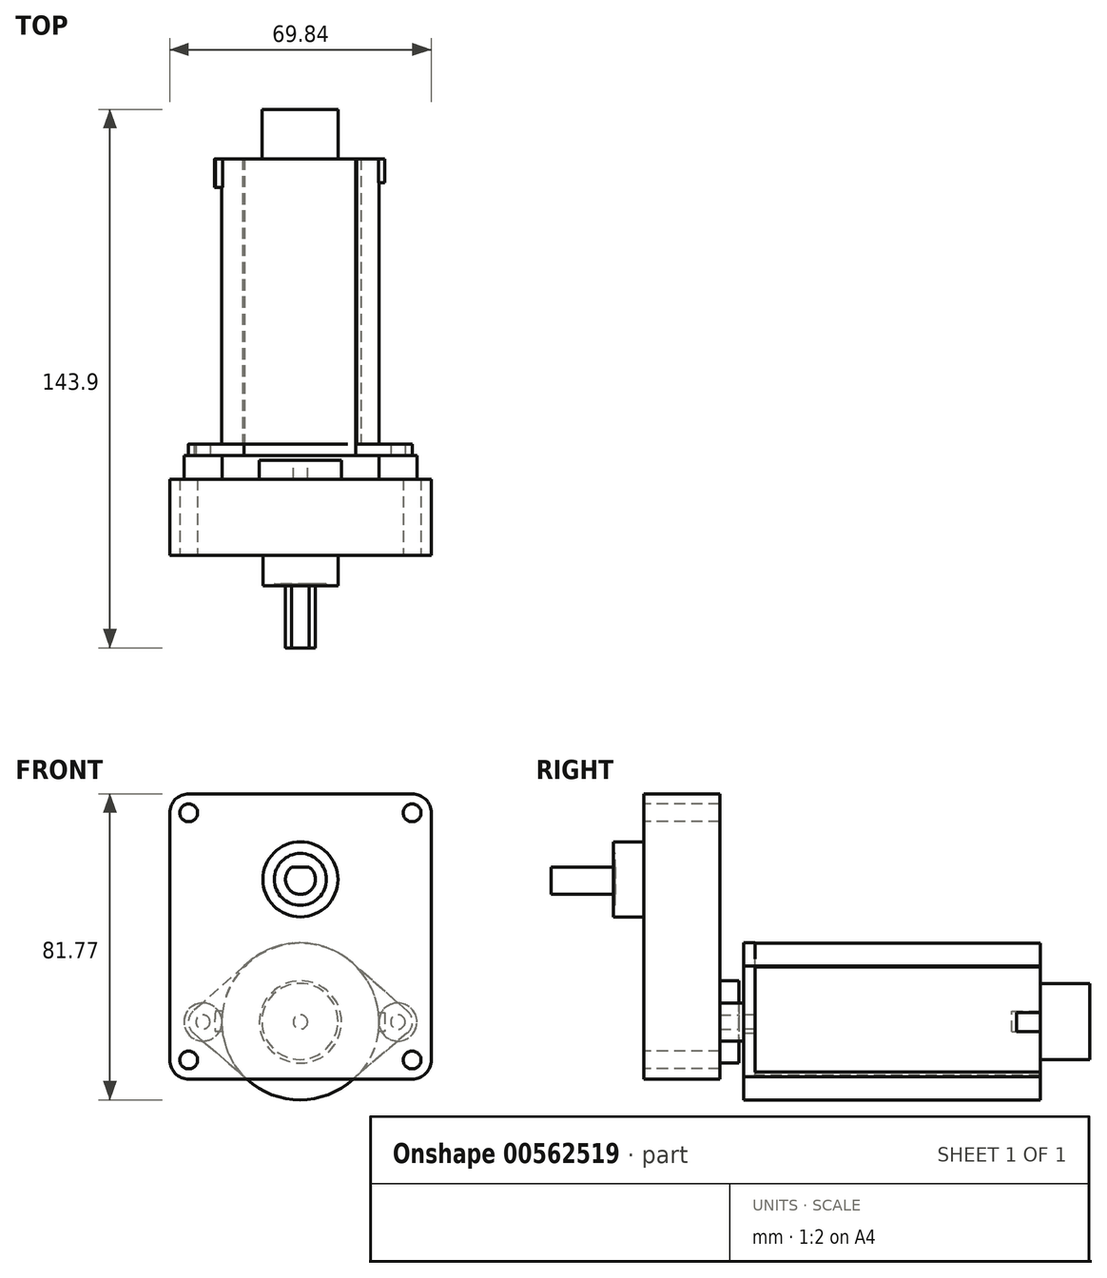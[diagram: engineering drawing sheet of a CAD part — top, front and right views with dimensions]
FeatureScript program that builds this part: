
annotation { "Feature Type Name" : "Feature", "Feature Type Description" : "" }
export const myFeature = defineFeature(function(context is Context, id is Id, definition is map)
    precondition{}
    {
        {
            var Q0;
            Q0=qCreatedBy(makeId("Front.planeOp"),FACE);
            var sketch = newSketch(context, id + "F0", { "sketchPlane" : qUnion([Q0])});
            skLineSegment(sketch, "E0.bottom", {"start": v(34.93, -38.1) * mm, "end": v(-34.92, -38.1) * mm});
            skLineSegment(sketch, "E0.top", {"start": v(34.92, 38.1) * mm, "end": v(-34.93, 38.1) * mm});
            skLineSegment(sketch, "E0.left", {"start": v(34.93, -38.1) * mm, "end": v(34.92, 38.1) * mm});
            skLineSegment(sketch, "E0.right", {"start": v(-34.92, -38.1) * mm, "end": v(-34.93, 38.1) * mm});
            skPoint(sketch, "E0.middle", {"position": v(0, 0) * mm});
            skSolve(sketch);
        }
        {
            var Q0;
            Q0=qSketchRegion(id+"F0",true);
            extrude(context, id + "F1", {"entities" : qUnion([Q0]), "depth" : 20.32 * mm, "offsetDistance" : 25.4 * mm});
        }
        {
            var Q0;
            Q0=makeQuery(id+"F1.opExtrude","SWEPT_EDGE",EDGE,{"disambiguationData":[OSD([sQuery(id+"F0.wireOp",EDGE,"E0.top"),sQuery(id+"F0.wireOp",EDGE,"E0.right")])]});
            var Q1;
            Q1=makeQuery(id+"F1.opExtrude","SWEPT_EDGE",EDGE,{"disambiguationData":[OSD([sQuery(id+"F0.wireOp",EDGE,"E0.bottom"),sQuery(id+"F0.wireOp",EDGE,"E0.right")])]});
            var Q2;
            Q2=makeQuery(id+"F1.opExtrude","SWEPT_EDGE",EDGE,{"disambiguationData":[OSD([sQuery(id+"F0.wireOp",EDGE,"E0.bottom"),sQuery(id+"F0.wireOp",EDGE,"E0.left")])]});
            var Q3;
            Q3=makeQuery(id+"F1.opExtrude","SWEPT_EDGE",EDGE,{"disambiguationData":[OSD([sQuery(id+"F0.wireOp",EDGE,"E0.top"),sQuery(id+"F0.wireOp",EDGE,"E0.left")])]});
            fillet(context, id + "F2", {"entities" : qUnion([Q0, Q1, Q2, Q3]), "radius" : 5.08 * mm, "tangentPropagation" : true, "allowEdgeOverflow" : false});
        }
        {
            var Q0;
            Q0=makeQuery(id+"F1.opExtrude","CAP_FACE",FACE,{"disambiguationData":[OSD([sQuery(id+"F0.wireOp",EDGE,"E0.bottom"),sQuery(id+"F0.wireOp",EDGE,"E0.top"),sQuery(id+"F0.wireOp",EDGE,"E0.left"),sQuery(id+"F0.wireOp",EDGE,"E0.right")])],"isStart":false});
            var sketch = newSketch(context, id + "F3", { "sketchPlane" : qUnion([Q0])});
            skPoint(sketch, "E1.middle", {"position": v(0, 0) * mm});
            skCircle(sketch, "E2", {"center": v(-29.84, 33.02) * mm, "radius": 2.37 * mm});
            skCircle(sketch, "E3", {"center": v(29.84, 33.02) * mm, "radius": 2.37 * mm});
            skCircle(sketch, "E4", {"center": v(29.84, -33.02) * mm, "radius": 2.37 * mm});
            skCircle(sketch, "E5", {"center": v(-29.84, -33.02) * mm, "radius": 2.37 * mm});
            skSolve(sketch);
        }
        {
            var Q0;
            Q0=makeQuery(id+"F3.imprint","IMPRINT",FACE,{"disambiguationData":[TD([[makeQuery(id+"F3.imprint","IMPRINT",EDGE,{"derivedFrom":sQuery(id+"F3.wireOp",EDGE,"E2")}),1.0]])]});
            var Q1;
            Q1=makeQuery(id+"F3.imprint","IMPRINT",FACE,{"disambiguationData":[TD([[makeQuery(id+"F3.imprint","IMPRINT",EDGE,{"derivedFrom":sQuery(id+"F3.wireOp",EDGE,"E3")}),1.0]])]});
            var Q2;
            Q2=makeQuery(id+"F3.imprint","IMPRINT",FACE,{"disambiguationData":[TD([[makeQuery(id+"F3.imprint","IMPRINT",EDGE,{"derivedFrom":sQuery(id+"F3.wireOp",EDGE,"E5")}),1.0]])]});
            var Q3;
            Q3=makeQuery(id+"F3.imprint","IMPRINT",FACE,{"disambiguationData":[TD([[makeQuery(id+"F3.imprint","IMPRINT",EDGE,{"derivedFrom":sQuery(id+"F3.wireOp",EDGE,"E4")}),1.0]])]});
            extrude(context, id + "F4", {"entities" : qUnion([Q0, Q1, Q2, Q3]), "operationType" : NewBodyOperationType.REMOVE, "endBound" : BoundingType.THROUGH_ALL, "oppositeDirection" : true, "depth" : 25.4 * mm, "offsetDistance" : 25.4 * mm});
        }
        {
            var Q0;
            Q0=makeQuery(id+"F1.opExtrude","CAP_FACE",FACE,{"disambiguationData":[OSD([sQuery(id+"F0.wireOp",EDGE,"E0.bottom"),sQuery(id+"F0.wireOp",EDGE,"E0.top"),sQuery(id+"F0.wireOp",EDGE,"E0.left"),sQuery(id+"F0.wireOp",EDGE,"E0.right")])],"isStart":false});
            var sketch = newSketch(context, id + "F5", { "sketchPlane" : qUnion([Q0])});
            skLineSegment(sketch, "E6", {"start": v(0, 0) * mm, "end": v(0, 38.1) * mm, "construction": true});
            skLineSegment(sketch, "E7", {"start": v(0, 15.24) * mm, "end": v(34.92, 15.24) * mm, "construction": true});
            skCircle(sketch, "E8", {"center": v(0, 15.24) * mm, "radius": 10.03 * mm});
            skSolve(sketch);
        }
        {
            var Q0;
            Q0=qSketchRegion(id+"F5",true);
            extrude(context, id + "F6", {"entities" : qUnion([Q0]), "operationType" : NewBodyOperationType.ADD, "depth" : 8.13 * mm, "offsetDistance" : 25.4 * mm});
        }
        {
            var Q0;
            Q0=makeQuery(id+"F6.opExtrude","CAP_FACE",FACE,{"disambiguationData":[OSD([sQuery(id+"F5.wireOp",EDGE,"E8")])],"isStart":false});
            var sketch = newSketch(context, id + "F7", { "sketchPlane" : qUnion([Q0])});
            skCircle(sketch, "E9", {"center": v(0, 15.24) * mm, "radius": 6.95 * mm});
            skSolve(sketch);
        }
        {
            var Q0;
            Q0=qSketchRegion(id+"F7",true);
            extrude(context, id + "F8", {"entities" : qUnion([Q0]), "operationType" : NewBodyOperationType.REMOVE, "oppositeDirection" : true, "depth" : 0.5 * mm, "offsetDistance" : 25.4 * mm});
        }
        {
            var Q0;
            Q0=makeQuery(id+"F8.boolean.opBoolean","COPY",FACE,{"derivedFrom":makeQuery(id+"F8.opExtrude","CAP_FACE",FACE,{"disambiguationData":[OSD([sQuery(id+"F7.wireOp",EDGE,"E9")])],"isStart":false})});
            var sketch = newSketch(context, id + "F9", { "sketchPlane" : qUnion([Q0])});
            skArc(sketch, "E10", {"start": v(-2.35, 18.48) * mm, "mid": v(0, 11.24) * mm, "end": v(2.35, 18.48) * mm});
            skLineSegment(sketch, "E11", {"start": v(-2.35, 18.48) * mm, "end": v(2.35, 18.48) * mm});
            skSolve(sketch);
        }
        {
            var Q0;
            Q0=makeQuery(id+"F9.imprint","IMPRINT",FACE,{"disambiguationData":[TD([[makeQuery(id+"F9.imprint","IMPRINT",EDGE,{"derivedFrom":sQuery(id+"F9.wireOp",EDGE,"E10")}),1.0]])]});
            extrude(context, id + "F10", {"entities" : qUnion([Q0]), "operationType" : NewBodyOperationType.ADD, "depth" : 17.14 * mm, "offsetDistance" : 25.4 * mm});
        }
        {
            var Q0;
            Q0=makeQuery(id+"F1.opExtrude","CAP_FACE",FACE,{"disambiguationData":[OSD([sQuery(id+"F0.wireOp",EDGE,"E0.bottom"),sQuery(id+"F0.wireOp",EDGE,"E0.top"),sQuery(id+"F0.wireOp",EDGE,"E0.left"),sQuery(id+"F0.wireOp",EDGE,"E0.right")])],"isStart":true});
            var sketch = newSketch(context, id + "F11", { "sketchPlane" : qUnion([Q0])});
            skLineSegment(sketch, "E12", {"start": v(-34.93, -22.86) * mm, "end": v(34.92, -22.86) * mm, "construction": true});
            skCircle(sketch, "E13", {"center": v(0, -22.86) * mm, "radius": 10.99 * mm});
            skLineSegment(sketch, "E14", {"start": v(26.03, -38.1) * mm, "end": v(26.04, 38.1) * mm, "construction": true});
            skLineSegment(sketch, "E15", {"start": v(-26.04, -38.1) * mm, "end": v(-26.04, 38.1) * mm, "construction": true});
            skCircle(sketch, "E16", {"center": v(-26.04, -22.86) * mm, "radius": 5.08 * mm});
            skCircle(sketch, "E17", {"center": v(26.03, -22.86) * mm, "radius": 5.08 * mm});
            skSolve(sketch);
        }
        {
            var Q0;
            Q0=makeQuery(id+"F11.imprint","IMPRINT",FACE,{"disambiguationData":[TD([[makeQuery(id+"F11.imprint","IMPRINT",EDGE,{"derivedFrom":sQuery(id+"F11.wireOp",EDGE,"E13")}),1.0]])]});
            extrude(context, id + "F12", {"entities" : qUnion([Q0]), "operationType" : NewBodyOperationType.ADD, "depth" : 5.08 * mm, "offsetDistance" : 25.4 * mm});
        }
        {
            var Q0;
            Q0=makeQuery(id+"F11.imprint","IMPRINT",FACE,{"disambiguationData":[TD([[makeQuery(id+"F11.imprint","IMPRINT",EDGE,{"derivedFrom":sQuery(id+"F11.wireOp",EDGE,"E17")}),1.0]])]});
            extrude(context, id + "F13", {"entities" : qUnion([Q0]), "operationType" : NewBodyOperationType.ADD, "depth" : 6.35 * mm, "offsetDistance" : 25.4 * mm});
        }
        {
            var Q0;
            Q0=makeQuery(id+"F11.imprint","IMPRINT",FACE,{"disambiguationData":[TD([[makeQuery(id+"F11.imprint","IMPRINT",EDGE,{"derivedFrom":sQuery(id+"F11.wireOp",EDGE,"E16")}),1.0]])]});
            extrude(context, id + "F14", {"entities" : qUnion([Q0]), "operationType" : NewBodyOperationType.ADD, "depth" : 6.35 * mm, "offsetDistance" : 25.4 * mm});
        }
        {
            var Q0;
            Q0=makeQuery(id+"F12.opExtrude","CAP_FACE",FACE,{"disambiguationData":[OSD([sQuery(id+"F11.wireOp",EDGE,"E13")])],"isStart":false});
            var sketch = newSketch(context, id + "F15", { "sketchPlane" : qUnion([Q0])});
            skCircle(sketch, "E18", {"center": v(0, -22.86) * mm, "radius": 1.9 * mm});
            skSolve(sketch);
        }
        {
            var Q0;
            Q0=makeQuery(id+"F15.imprint","IMPRINT",FACE,{"disambiguationData":[TD([[makeQuery(id+"F15.imprint","IMPRINT",EDGE,{"derivedFrom":sQuery(id+"F15.wireOp",EDGE,"E18")}),1.0]])]});
            extrude(context, id + "F16", {"entities" : qUnion([Q0]), "operationType" : NewBodyOperationType.REMOVE, "oppositeDirection" : true, "depth" : 5.08 * mm, "offsetDistance" : 25.4 * mm});
        }
        {
            var Q0;
            Q0=makeQuery(id+"F14.opExtrude","CAP_FACE",FACE,{"disambiguationData":[OSD([sQuery(id+"F11.wireOp",EDGE,"E16")])],"isStart":false});
            var sketch = newSketch(context, id + "F17", { "sketchPlane" : qUnion([Q0])});
            skCircle(sketch, "E19", {"center": v(-26.04, -22.86) * mm, "radius": 1.59 * mm});
            skCircle(sketch, "E20", {"center": v(26.03, -22.86) * mm, "radius": 1.59 * mm});
            skSolve(sketch);
        }
        {
            var Q0;
            Q0=makeQuery(id+"F17.imprint","IMPRINT",FACE,{"disambiguationData":[TD([[makeQuery(id+"F17.imprint","IMPRINT",EDGE,{"derivedFrom":sQuery(id+"F17.wireOp",EDGE,"E19")}),-1.0]])]});
            var sketch = newSketch(context, id + "F18", { "sketchPlane" : qUnion([Q0])});
            skCircle(sketch, "E21", {"center": v(-26.04, -22.86) * mm, "radius": 1.93 * mm});
            skCircle(sketch, "E22", {"center": v(26.03, -22.86) * mm, "radius": 1.89 * mm});
            skArc(sketch, "E23", {"start": v(-28.58, -19.92) * mm, "mid": v(-29.92, -22.89) * mm, "end": v(-28.54, -25.83) * mm});
            skArc(sketch, "E24", {"start": v(28.38, -25.96) * mm, "mid": v(29.92, -23.01) * mm, "end": v(28.62, -19.95) * mm});
            skLineSegment(sketch, "E25", {"start": v(-28.58, -19.92) * mm, "end": v(-14.74, -7.93) * mm});
            skLineSegment(sketch, "E26", {"start": v(-28.54, -25.83) * mm, "end": v(-14.74, -37.48) * mm});
            skArc(sketch, "E27.trimOffspring", {"start": v(-14.74, -37.48) * mm, "mid": v(0.08, -43.67) * mm, "end": v(14.94, -37.55) * mm});
            skPoint(sketch, "E28.center.orphan", {"position": v(0, -22.82) * mm});
            skPoint(sketch, "E29.end.orphan", {"position": v(15.07, -7.93) * mm});
            skPoint(sketch, "E30.end.orphan", {"position": v(15.07, -37.71) * mm});
            skLineSegment(sketch, "E31", {"start": v(28.38, -25.96) * mm, "end": v(14.94, -37.55) * mm});
            skLineSegment(sketch, "E32", {"start": v(15.03, -7.96) * mm, "end": v(28.62, -19.95) * mm});
            skArc(sketch, "E33.trimOffspring", {"start": v(15.03, -7.96) * mm, "mid": v(0.15, -1.74) * mm, "end": v(-14.74, -7.93) * mm});
            skSolve(sketch);
        }
        {
            var Q0;
            Q0=qSketchRegion(id+"F18",true);
            extrude(context, id + "F19", {"entities" : qUnion([Q0]), "operationType" : NewBodyOperationType.ADD, "depth" : 3.05 * mm, "offsetDistance" : 25.4 * mm});
        }
        {
            var Q0;
            Q0=makeQuery(id+"F19.opExtrude","CAP_FACE",FACE,{"disambiguationData":[OSD([sQuery(id+"F18.wireOp",EDGE,"E21"),sQuery(id+"F18.wireOp",EDGE,"E22"),sQuery(id+"F18.wireOp",EDGE,"E23"),sQuery(id+"F18.wireOp",EDGE,"E24"),sQuery(id+"F18.wireOp",EDGE,"E25"),sQuery(id+"F18.wireOp",EDGE,"E26"),sQuery(id+"F18.wireOp",EDGE,"E27.trimOffspring"),sQuery(id+"F18.wireOp",EDGE,"E31"),sQuery(id+"F18.wireOp",EDGE,"E32"),sQuery(id+"F18.wireOp",EDGE,"E33.trimOffspring")])],"isStart":false});
            var sketch = newSketch(context, id + "F20", { "sketchPlane" : qUnion([Q0])});
            skCircle(sketch, "E34", {"center": v(0, -22.86) * mm, "radius": 21.01 * mm});
            skCircle(sketch, "E35", {"center": v(-26.04, -22.86) * mm, "radius": 3.7 * mm});
            skCircle(sketch, "E36", {"center": v(26.03, -22.86) * mm, "radius": 3.68 * mm});
            skSolve(sketch);
        }
        {
            var Q0;
            {var subQ0=makeQuery(id+"F19.opExtrude","CAP_EDGE",EDGE,{"disambiguationData":[OSD([sQuery(id+"F18.wireOp",EDGE,"E27.trimOffspring")])],"isStart":false});Q0=makeQuery(id+"F20.imprint","IMPRINT",FACE,{"disambiguationData":[TD([[makeQuery(id+"F20.imprint","IMPRINT",EDGE,{"derivedFrom":subQ0}),1.0]])]});}
            extrude(context, id + "F21", {"entities" : qUnion([Q0]), "operationType" : NewBodyOperationType.ADD, "depth" : 76.2 * mm, "offsetDistance" : 25.4 * mm});
        }
        {
            var Q0;
            Q0=makeQuery(id+"F21.opExtrude","CAP_FACE",FACE,{"disambiguationData":[OSD([sQuery(id+"F18.wireOp",EDGE,"E25"),sQuery(id+"F18.wireOp",EDGE,"E26"),sQuery(id+"F18.wireOp",EDGE,"E27.trimOffspring"),sQuery(id+"F18.wireOp",EDGE,"E31"),sQuery(id+"F18.wireOp",EDGE,"E33.trimOffspring"),sQuery(id+"F20.wireOp",EDGE,"E34")])],"isStart":false});
            var sketch = newSketch(context, id + "F22", { "sketchPlane" : qUnion([Q0])});
            skCircle(sketch, "E37", {"center": v(0.13, -22.7) * mm, "radius": 10.16 * mm});
            skSolve(sketch);
        }
        {
            var Q0;
            Q0=qSketchRegion(id+"F22",true);
            extrude(context, id + "F23", {"entities" : qUnion([Q0]), "operationType" : NewBodyOperationType.ADD, "depth" : 13.2 * mm, "offsetDistance" : 25.4 * mm});
        }
        {
            var Q0;
            Q0=makeQuery(id+"F21.opExtrude","CAP_FACE",FACE,{"disambiguationData":[OSD([sQuery(id+"F18.wireOp",EDGE,"E25"),sQuery(id+"F18.wireOp",EDGE,"E26"),sQuery(id+"F18.wireOp",EDGE,"E27.trimOffspring"),sQuery(id+"F18.wireOp",EDGE,"E31"),sQuery(id+"F18.wireOp",EDGE,"E33.trimOffspring"),sQuery(id+"F20.wireOp",EDGE,"E34")])],"isStart":false});
            var sketch = newSketch(context, id + "F24", { "sketchPlane" : qUnion([Q0])});
            skArc(sketch, "E38", {"start": v(-22.76, -20.35) * mm, "mid": v(-22.9, -22.69) * mm, "end": v(-22.8, -25.03) * mm});
            skLineSegment(sketch, "E39", {"start": v(20.8, -19.95) * mm, "end": v(22.7, -19.95) * mm});
            skLineSegment(sketch, "E40", {"start": v(20.85, -25.46) * mm, "end": v(22.75, -25.46) * mm});
            skLineSegment(sketch, "E41", {"start": v(-20.86, -20.35) * mm, "end": v(-22.76, -20.35) * mm});
            skLineSegment(sketch, "E42", {"start": v(-20.9, -25.03) * mm, "end": v(-22.8, -25.03) * mm});
            skArc(sketch, "E43.trimOffspring", {"start": v(22.75, -25.46) * mm, "mid": v(22.9, -22.7) * mm, "end": v(22.7, -19.95) * mm});
            skSolve(sketch);
        }
        {
            var Q0;
            {var subQ0=sQuery(id+"F24.wireOp",EDGE,"E39");Q0=makeQuery(id+"F24.imprint","IMPRINT",FACE,{"disambiguationData":[TD([[makeQuery(id+"F24.imprint","IMPRINT",EDGE,{"derivedFrom":subQ0}),-1.0]])]});}
            extrude(context, id + "F25", {"entities" : qUnion([Q0]), "operationType" : NewBodyOperationType.ADD, "oppositeDirection" : true, "depth" : 7.62 * mm, "offsetDistance" : 25.4 * mm});
        }
        {
            var Q0;
            {var subQ0=sQuery(id+"F20.wireOp",EDGE,"E34");Q0=makeQuery(id+"F25.boolean.opBoolean","MERGE",FACE,{"derivedFrom":[makeQuery(id+"F21.opExtrude","CAP_FACE",FACE,{"disambiguationData":[OSD([sQuery(id+"F18.wireOp",EDGE,"E25"),sQuery(id+"F18.wireOp",EDGE,"E26"),sQuery(id+"F18.wireOp",EDGE,"E27.trimOffspring"),sQuery(id+"F18.wireOp",EDGE,"E31"),sQuery(id+"F18.wireOp",EDGE,"E33.trimOffspring"),subQ0])],"isStart":false}),makeQuery(id+"F25.opExtrude","CAP_FACE",FACE,{"disambiguationData":[OSD([subQ0,sQuery(id+"F24.wireOp",EDGE,"E39"),sQuery(id+"F24.wireOp",EDGE,"E40"),sQuery(id+"F24.wireOp",EDGE,"E43.trimOffspring")])],"isStart":true})]});}
            var sketch = newSketch(context, id + "F26", { "sketchPlane" : qUnion([Q0])});
            skLineSegment(sketch, "E44", {"start": v(-20.87, -20.38) * mm, "end": v(-22.48, -20.38) * mm});
            skLineSegment(sketch, "E45", {"start": v(-22.48, -20.38) * mm, "end": v(-22.48, -25.46) * mm});
            skLineSegment(sketch, "E46", {"start": v(-22.48, -25.46) * mm, "end": v(-20.85, -25.46) * mm});
            skSolve(sketch);
        }
        {
            var Q0;
            Q0=qSketchRegion(id+"F26",true);
            var Q1;
            {var subQ0=sQuery(id+"F26.wireOp",EDGE,"E44");Q1=makeQuery(id+"F26.imprint","IMPRINT",FACE,{"disambiguationData":[TD([[makeQuery(id+"F26.imprint","IMPRINT",EDGE,{"derivedFrom":subQ0}),1.0]])]});}
            extrude(context, id + "F27", {"entities" : qUnion([Q0, Q1]), "operationType" : NewBodyOperationType.ADD, "oppositeDirection" : true, "depth" : 6.35 * mm, "offsetDistance" : 25.4 * mm});
        }
    });
